# Revit family: Hand Dryer_Metlam_Eclipse
name_source: partatom
category: Specialty Equipment
revit_build: Autodesk Revit 2016 (Build: 20170117_1200(x64)
units: mm (PartAtom-declared; Revit-internal decimal feet)

## family parameters
Always vertical = Yes
Cut with Voids When Loaded = No
OmniClass Number = 23.40.20.21.14
OmniClass Title = Hand and Hair Dryers
Part Type = Normal
Room Calculation Point = Yes
Round Connector Dimension = Use Diameter
Shared = No
Work Plane-Based = No

## types (2) — shared parameters
Description = Auto Operation Hand Dryer
Manufacturer = Metlam
Manufacturer_Overall Depth = 100 mm  [stored 0.328084 ft]
Manufacturer_Overall Height = 288 mm
Manufacturer_Overall Width = 220 mm  [stored 0.721785 ft]
Manufacturer_URL__Product Specific = https://metlam.com.au
Type Comments = Hand Dryers
URL = http://www.metlam.com.au
Voltage = 240 V

## per-type parameters (varying)
| type | Manufacturer_Spec Code | Material_ANZRS | Model |
| Satin 220w x 100d x 288h (ML_ECLIPSE05_SS) | ML_ECLIPSE05_SS | z_Metlam_Metal_Stainless Steel_Satin | ML_ECLIPSE05_SS |
| White 220w x 100d x 288h (ML_ECLIPSE01_WHT) | ML_ECLIPSE01_WHT | z_Metlam_White | ML_ECLIPSE01_WHT |

note: [stored X ft] marks values corroborated as IEEE doubles in the binary element streams (Revit-internal decimal feet)

## geometry (parser evidence)
native form markers: Sweep x3
no freeform markers — native parametric forms only
